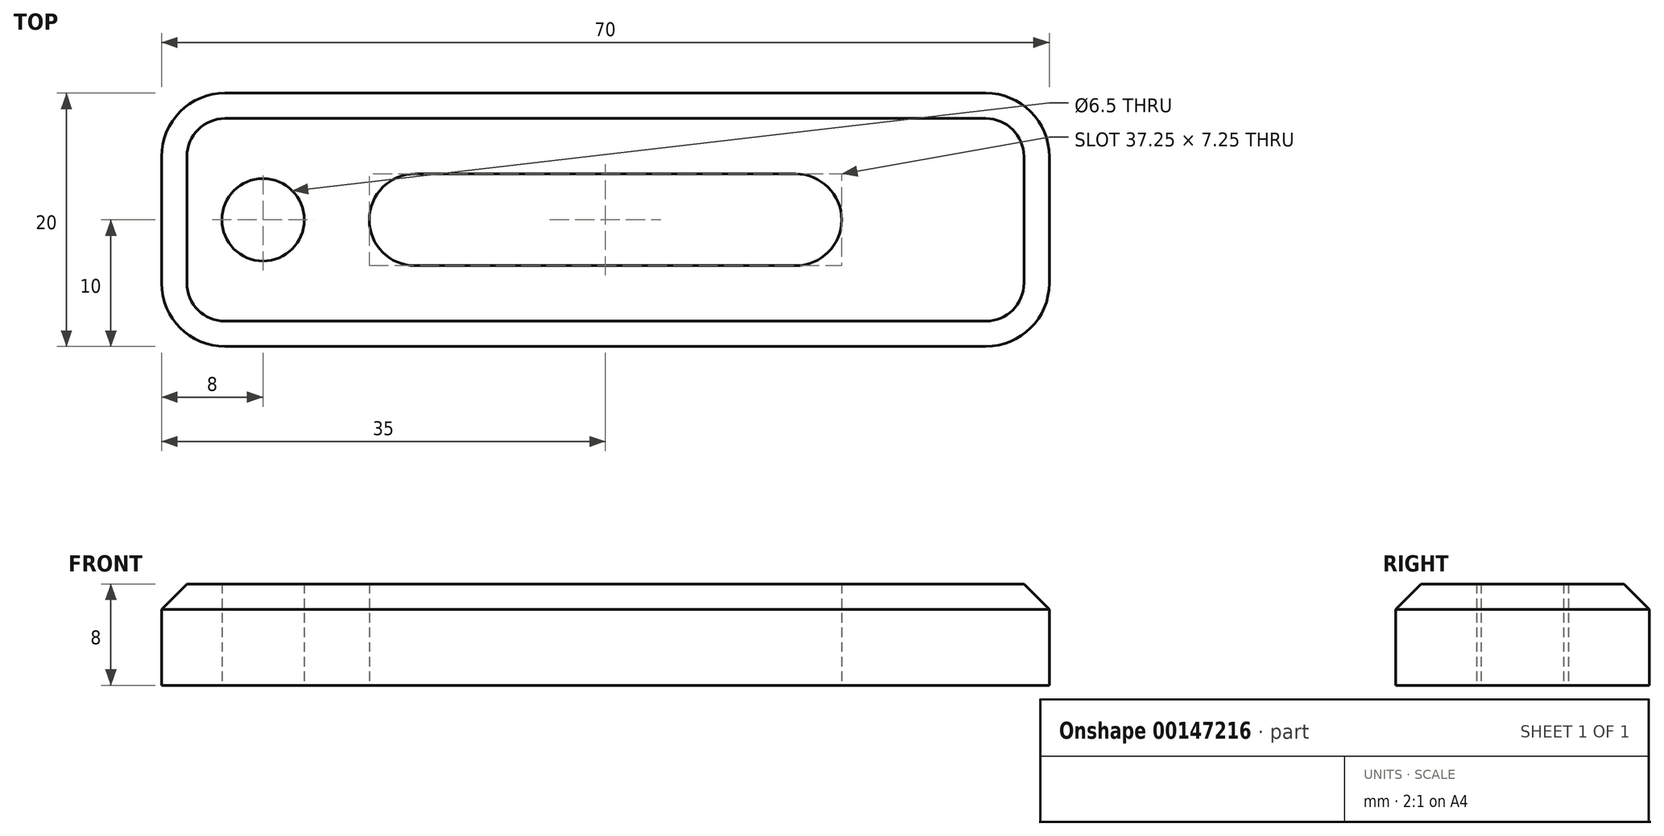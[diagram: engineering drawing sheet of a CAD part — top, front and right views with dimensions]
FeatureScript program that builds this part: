
annotation { "Feature Type Name" : "Feature", "Feature Type Description" : "" }
export const myFeature = defineFeature(function(context is Context, id is Id, definition is map)
    precondition{}
    {
        {
            var Q0;
            Q0=qCreatedBy(makeId("Top.planeOp"),FACE);
            var sketch = newSketch(context, id + "F0", { "sketchPlane" : qUnion([Q0])});
            skLineSegment(sketch, "E0.bottom", {"start": v(35, -10) * mm, "end": v(-35, -10) * mm});
            skLineSegment(sketch, "E0.top", {"start": v(35, 10) * mm, "end": v(-35, 10) * mm});
            skLineSegment(sketch, "E0.left", {"start": v(35, -10) * mm, "end": v(35, 10) * mm});
            skLineSegment(sketch, "E0.right", {"start": v(-35, -10) * mm, "end": v(-35, 10) * mm});
            skPoint(sketch, "E0.middle", {"position": v(0, 0) * mm});
            skCircle(sketch, "E1", {"center": v(-27, 0) * mm, "radius": 3.25 * mm});
            skCircle(sketch, "E2", {"center": v(-15, 0) * mm, "radius": 3.62 * mm});
            skCircle(sketch, "E3", {"center": v(15, 0) * mm, "radius": 3.62 * mm});
            skLineSegment(sketch, "E4", {"start": v(-15, 3.63) * mm, "end": v(15, 3.63) * mm});
            skLineSegment(sketch, "E5", {"start": v(-15, -3.62) * mm, "end": v(15, -3.62) * mm});
            skSolve(sketch);
        }
        {
            var Q0;
            Q0=qSketchRegion(id+"F0",true);
            extrude(context, id + "F1", {"entities" : qUnion([Q0]), "depth" : 8 * mm});
        }
        {
            var Q0;
            Q0=makeQuery(id+"F1.opExtrude","SWEPT_EDGE",EDGE,{"disambiguationData":[OSD([sQuery(id+"F0.wireOp",EDGE,"E0.bottom"),sQuery(id+"F0.wireOp",EDGE,"E0.right")])]});
            var Q1;
            Q1=makeQuery(id+"F1.opExtrude","SWEPT_EDGE",EDGE,{"disambiguationData":[OSD([sQuery(id+"F0.wireOp",EDGE,"E0.bottom"),sQuery(id+"F0.wireOp",EDGE,"E0.left")])]});
            var Q2;
            Q2=makeQuery(id+"F1.opExtrude","SWEPT_EDGE",EDGE,{"disambiguationData":[OSD([sQuery(id+"F0.wireOp",EDGE,"E0.top"),sQuery(id+"F0.wireOp",EDGE,"E0.left")])]});
            var Q3;
            Q3=makeQuery(id+"F1.opExtrude","SWEPT_EDGE",EDGE,{"disambiguationData":[OSD([sQuery(id+"F0.wireOp",EDGE,"E0.top"),sQuery(id+"F0.wireOp",EDGE,"E0.right")])]});
            fillet(context, id + "F2", {"entities" : qUnion([Q0, Q1, Q2, Q3]), "radius" : 5 * mm, "tangentPropagation" : true, "allowEdgeOverflow" : false});
        }
        {
            var Q0;
            Q0=makeQuery(id+"F1.opExtrude","CAP_EDGE",EDGE,{"disambiguationData":[OSD([sQuery(id+"F0.wireOp",EDGE,"E0.bottom")])],"isStart":false});
            chamfer(context, id + "F3", {"entities" : qUnion([Q0]), "width" : 2 * mm, "tangentPropagation" : true});
        }
    });
